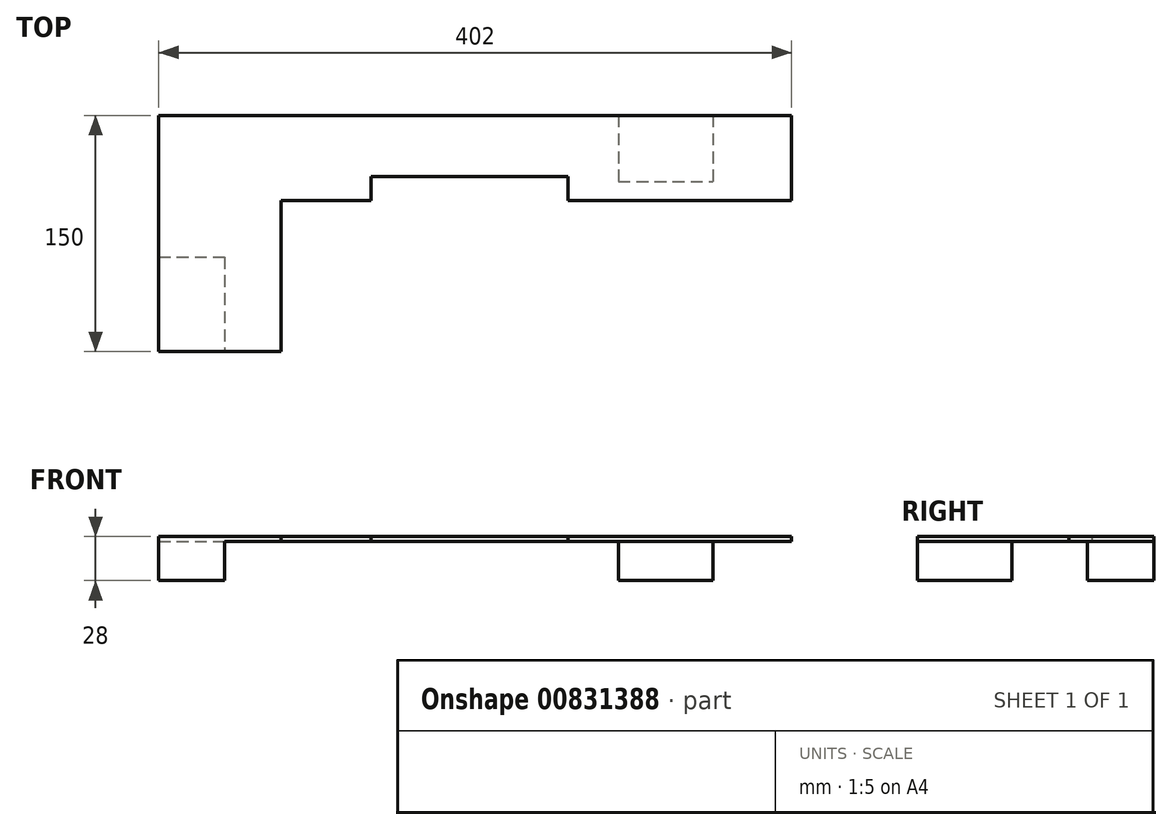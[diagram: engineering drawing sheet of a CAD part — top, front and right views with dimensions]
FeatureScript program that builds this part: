
annotation { "Feature Type Name" : "Feature", "Feature Type Description" : "" }
export const myFeature = defineFeature(function(context is Context, id is Id, definition is map)
    precondition{}
    {
        {
            var Q0;
            Q0=qCreatedBy(makeId("Top.planeOp"),FACE);
            var sketch = newSketch(context, id + "F0", { "sketchPlane" : qUnion([Q0])});
            skLineSegment(sketch, "E0", {"start": v(0, -96) * mm, "end": v(0, 0) * mm});
            skLineSegment(sketch, "E1", {"start": v(0, 0) * mm, "end": v(324.3, 0) * mm});
            skLineSegment(sketch, "E2", {"start": v(324.3, 0) * mm, "end": v(324.3, 54) * mm});
            skLineSegment(sketch, "E3", {"start": v(324.3, 54) * mm, "end": v(-77.7, 54) * mm});
            skLineSegment(sketch, "E4", {"start": v(-77.7, 54) * mm, "end": v(-77.7, -96) * mm});
            skLineSegment(sketch, "E5", {"start": v(-77.7, -96) * mm, "end": v(0, -96) * mm});
            skSolve(sketch);
        }
        {
            var Q0;
            Q0=makeQuery(id+"F0.imprint","IMPRINT",FACE,{"disambiguationData":[TD([[makeQuery(id+"F0.imprint","IMPRINT",EDGE,{"derivedFrom":sQuery(id+"F0.wireOp",EDGE,"E0")}),1.0]])]});
            extrude(context, id + "F1", {"entities" : qUnion([Q0]), "endBound" : BoundingType.SYMMETRIC, "depth" : 3 * mm, "offsetDistance" : 25 * mm});
        }
        {
            var Q0;
            Q0=makeQuery(id+"F1.opExtrude","SWEPT_FACE",FACE,{"disambiguationData":[OSD([sQuery(id+"F0.wireOp",EDGE,"E5")])]});
            var sketch = newSketch(context, id + "F2", { "sketchPlane" : qUnion([Q0])});
            skLineSegment(sketch, "E6.bottom", {"start": v(-77.7, -1.5) * mm, "end": v(-35.7, -1.5) * mm});
            skLineSegment(sketch, "E6.top", {"start": v(-77.7, -26.5) * mm, "end": v(-35.7, -26.5) * mm});
            skLineSegment(sketch, "E6.left", {"start": v(-77.7, -1.5) * mm, "end": v(-77.7, -26.5) * mm});
            skLineSegment(sketch, "E6.right", {"start": v(-35.7, -1.5) * mm, "end": v(-35.7, -26.5) * mm});
            skSolve(sketch);
        }
        {
            var Q0;
            Q0 = qSketchRegion(id + "F2", true);
            extrude(context, id + "F3", {"entities" : qUnion([Q0]), "operationType" : NewBodyOperationType.ADD, "oppositeDirection" : true, "depth" : 60 * mm, "offsetDistance" : 25 * mm});
        }
        {
            var Q0;
            Q0=makeQuery(id+"F1.opExtrude","SWEPT_FACE",FACE,{"disambiguationData":[OSD([sQuery(id+"F0.wireOp",EDGE,"E2")])]});
            cPlane(context, id + "F4", {"entities" : qUnion([Q0]), "cplaneType" : CPlaneType.OFFSET, "offset" : 50 * mm, "oppositeDirection" : true, "width" : 150 * mm, "height" : 150 * mm});
        }
        {
            var Q0;
            Q0=qCreatedBy(id+"F4.planeOp",FACE);
            var sketch = newSketch(context, id + "F5", { "sketchPlane" : qUnion([Q0])});
            skLineSegment(sketch, "E7.bottom", {"start": v(54, -1.5) * mm, "end": v(12, -1.5) * mm});
            skLineSegment(sketch, "E7.top", {"start": v(54, -26.5) * mm, "end": v(12, -26.5) * mm});
            skLineSegment(sketch, "E7.left", {"start": v(54, -1.5) * mm, "end": v(54, -26.5) * mm});
            skLineSegment(sketch, "E7.right", {"start": v(12, -1.5) * mm, "end": v(12, -26.5) * mm});
            skSolve(sketch);
        }
        {
            var Q0;
            Q0=makeQuery(id+"F5.imprint","IMPRINT",FACE,{"disambiguationData":[TD([[makeQuery(id+"F5.imprint","IMPRINT",EDGE,{"derivedFrom":sQuery(id+"F5.wireOp",EDGE,"E7.bottom")}),1.0]])]});
            extrude(context, id + "F6", {"entities" : qUnion([Q0]), "operationType" : NewBodyOperationType.ADD, "oppositeDirection" : true, "depth" : 60 * mm, "offsetDistance" : 25 * mm});
        }
        {
            var Q0;
            Q0=makeQuery(id+"F1.opExtrude","CAP_FACE",FACE,{"disambiguationData":[OSD([sQuery(id+"F0.wireOp",EDGE,"E0"),sQuery(id+"F0.wireOp",EDGE,"E1"),sQuery(id+"F0.wireOp",EDGE,"E2"),sQuery(id+"F0.wireOp",EDGE,"E3"),sQuery(id+"F0.wireOp",EDGE,"E4"),sQuery(id+"F0.wireOp",EDGE,"E5")])],"isStart":false});
            var sketch = newSketch(context, id + "F7", { "sketchPlane" : qUnion([Q0])});
            skLineSegment(sketch, "E8.bottom", {"start": v(57.3, 0) * mm, "end": v(182.3, 0) * mm});
            skLineSegment(sketch, "E8.top", {"start": v(57.3, 15) * mm, "end": v(182.3, 15) * mm});
            skLineSegment(sketch, "E8.left", {"start": v(57.3, 0) * mm, "end": v(57.3, 15) * mm});
            skLineSegment(sketch, "E8.right", {"start": v(182.3, 0) * mm, "end": v(182.3, 15) * mm});
            skSolve(sketch);
        }
        {
            var Q0;
            Q0=makeQuery(id+"F7.imprint","IMPRINT",FACE,{"disambiguationData":[TD([[makeQuery(id+"F7.imprint","IMPRINT",EDGE,{"derivedFrom":sQuery(id+"F7.wireOp",EDGE,"E8.bottom")}),1.0]])]});
            extrude(context, id + "F8", {"entities" : qUnion([Q0]), "operationType" : NewBodyOperationType.REMOVE, "oppositeDirection" : true, "depth" : 25 * mm, "offsetDistance" : 25 * mm});
        }
    });
